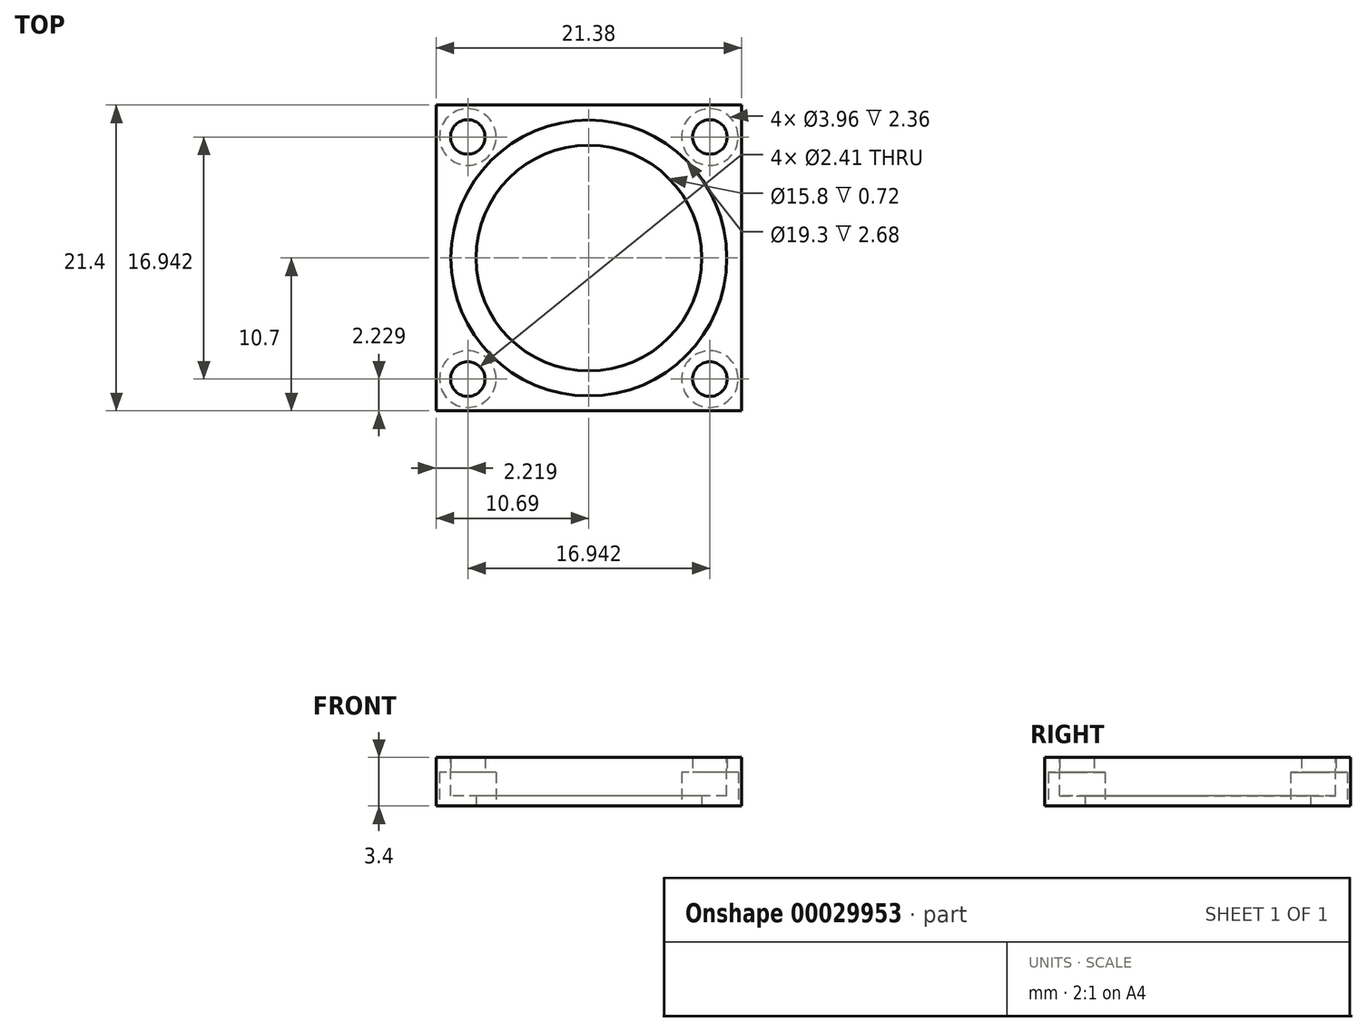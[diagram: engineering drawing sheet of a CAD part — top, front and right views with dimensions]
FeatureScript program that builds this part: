
annotation { "Feature Type Name" : "Feature", "Feature Type Description" : "" }
export const myFeature = defineFeature(function(context is Context, id is Id, definition is map)
    precondition{}
    {
        {
            var Q0;
            Q0=qCreatedBy(makeId("Top.planeOp"),FACE);
            var sketch = newSketch(context, id + "F0", { "sketchPlane" : qUnion([Q0])});
            skCircle(sketch, "E0", {"center": v(-8.47, 8.47) * mm, "radius": 1.2 * mm});
            skLineSegment(sketch, "E1.rect.bottom", {"start": v(-10.69, 10.7) * mm, "end": v(10.7, 10.7) * mm});
            skLineSegment(sketch, "E1.rect.top", {"start": v(-10.7, -10.7) * mm, "end": v(10.7, -10.7) * mm});
            skLineSegment(sketch, "E1.rect.left", {"start": v(-10.69, 10.7) * mm, "end": v(-10.7, -10.7) * mm});
            skLineSegment(sketch, "E1.rect.right", {"start": v(10.7, 10.7) * mm, "end": v(10.7, -10.7) * mm});
            skPoint(sketch, "E1.rect.middle", {"position": v(0, 0) * mm});
            skCircle(sketch, "E2", {"center": v(-8.47, 8.47) * mm, "radius": 1.98 * mm});
            skLineSegment(sketch, "E3.rect.bottom", {"start": v(-8.47, 8.47) * mm, "end": v(8.47, 8.47) * mm, "construction": true});
            skLineSegment(sketch, "E3.rect.top", {"start": v(-8.47, -8.47) * mm, "end": v(8.47, -8.47) * mm, "construction": true});
            skLineSegment(sketch, "E3.rect.left", {"start": v(-8.47, 8.47) * mm, "end": v(-8.47, -8.47) * mm, "construction": true});
            skLineSegment(sketch, "E3.rect.right", {"start": v(8.47, 8.47) * mm, "end": v(8.47, -8.47) * mm, "construction": true});
            skCircle(sketch, "E4.0.1.0", {"center": v(-8.47, -8.47) * mm, "radius": 1.2 * mm});
            skCircle(sketch, "E4.0.1.1", {"center": v(-8.47, -8.47) * mm, "radius": 1.98 * mm});
            skCircle(sketch, "E4.1.0.0", {"center": v(8.47, 8.47) * mm, "radius": 1.2 * mm});
            skCircle(sketch, "E4.1.0.1", {"center": v(8.47, 8.47) * mm, "radius": 1.98 * mm});
            skCircle(sketch, "E4.1.1.0", {"center": v(8.47, -8.47) * mm, "radius": 1.2 * mm});
            skCircle(sketch, "E4.1.1.1", {"center": v(8.47, -8.47) * mm, "radius": 1.98 * mm});
            skCircle(sketch, "E5", {"center": v(0, 0) * mm, "radius": 7.9 * mm});
            skSolve(sketch);
        }
        {
            var Q0;
            Q0=makeQuery(id+"F0.imprint","IMPRINT",FACE,{"disambiguationData":[TD([[makeQuery(id+"F0.imprint","IMPRINT",EDGE,{"derivedFrom":sQuery(id+"F0.wireOp",EDGE,"E1.rect.bottom")}),-1.0]])]});
            var Q1;
            Q1=makeQuery(id+"F0.imprint","IMPRINT",FACE,{"disambiguationData":[TD([[makeQuery(id+"F0.imprint","IMPRINT",EDGE,{"derivedFrom":sQuery(id+"F0.wireOp",EDGE,"E4.0.1.0")}),-1.0]])]});
            var Q2;
            Q2=makeQuery(id+"F0.imprint","IMPRINT",FACE,{"disambiguationData":[TD([[makeQuery(id+"F0.imprint","IMPRINT",EDGE,{"derivedFrom":sQuery(id+"F0.wireOp",EDGE,"E4.0.1.0")}),1.0]])]});
            var Q3;
            Q3=makeQuery(id+"F0.imprint","IMPRINT",FACE,{"disambiguationData":[TD([[makeQuery(id+"F0.imprint","IMPRINT",EDGE,{"derivedFrom":sQuery(id+"F0.wireOp",EDGE,"E4.1.1.0")}),1.0]])]});
            var Q4;
            Q4=makeQuery(id+"F0.imprint","IMPRINT",FACE,{"disambiguationData":[TD([[makeQuery(id+"F0.imprint","IMPRINT",EDGE,{"derivedFrom":sQuery(id+"F0.wireOp",EDGE,"E4.1.1.0")}),-1.0]])]});
            var Q5;
            Q5=makeQuery(id+"F0.imprint","IMPRINT",FACE,{"disambiguationData":[TD([[makeQuery(id+"F0.imprint","IMPRINT",EDGE,{"derivedFrom":sQuery(id+"F0.wireOp",EDGE,"E4.1.0.0")}),-1.0]])]});
            var Q6;
            Q6=makeQuery(id+"F0.imprint","IMPRINT",FACE,{"disambiguationData":[TD([[makeQuery(id+"F0.imprint","IMPRINT",EDGE,{"derivedFrom":sQuery(id+"F0.wireOp",EDGE,"E4.1.0.0")}),1.0]])]});
            var Q7;
            Q7=makeQuery(id+"F0.imprint","IMPRINT",FACE,{"disambiguationData":[TD([[makeQuery(id+"F0.imprint","IMPRINT",EDGE,{"derivedFrom":sQuery(id+"F0.wireOp",EDGE,"E0")}),1.0]])]});
            var Q8;
            Q8=makeQuery(id+"F0.imprint","IMPRINT",FACE,{"disambiguationData":[TD([[makeQuery(id+"F0.imprint","IMPRINT",EDGE,{"derivedFrom":sQuery(id+"F0.wireOp",EDGE,"E0")}),-1.0]])]});
            extrude(context, id + "F1", {"entities" : qUnion([Q0, Q1, Q2, Q3, Q4, Q5, Q6, Q7, Q8]), "depth" : 3.4 * mm});
        }
        {
            var Q0;
            Q0=makeQuery(id+"F0.imprint","IMPRINT",FACE,{"disambiguationData":[TD([[makeQuery(id+"F0.imprint","IMPRINT",EDGE,{"derivedFrom":sQuery(id+"F0.wireOp",EDGE,"E4.0.1.0")}),-1.0]])]});
            var Q1;
            Q1=makeQuery(id+"F0.imprint","IMPRINT",FACE,{"disambiguationData":[TD([[makeQuery(id+"F0.imprint","IMPRINT",EDGE,{"derivedFrom":sQuery(id+"F0.wireOp",EDGE,"E0")}),-1.0]])]});
            var Q2;
            Q2=makeQuery(id+"F0.imprint","IMPRINT",FACE,{"disambiguationData":[TD([[makeQuery(id+"F0.imprint","IMPRINT",EDGE,{"derivedFrom":sQuery(id+"F0.wireOp",EDGE,"E4.1.1.0")}),-1.0]])]});
            var Q3;
            Q3=makeQuery(id+"F0.imprint","IMPRINT",FACE,{"disambiguationData":[TD([[makeQuery(id+"F0.imprint","IMPRINT",EDGE,{"derivedFrom":sQuery(id+"F0.wireOp",EDGE,"E4.1.0.0")}),-1.0]])]});
            var Q4;
            Q4=makeQuery(id+"F0.imprint","IMPRINT",FACE,{"disambiguationData":[TD([[makeQuery(id+"F0.imprint","IMPRINT",EDGE,{"derivedFrom":sQuery(id+"F0.wireOp",EDGE,"E4.0.1.0")}),1.0]])]});
            var Q5;
            Q5=makeQuery(id+"F0.imprint","IMPRINT",FACE,{"disambiguationData":[TD([[makeQuery(id+"F0.imprint","IMPRINT",EDGE,{"derivedFrom":sQuery(id+"F0.wireOp",EDGE,"E4.1.1.0")}),1.0]])]});
            var Q6;
            Q6=makeQuery(id+"F0.imprint","IMPRINT",FACE,{"disambiguationData":[TD([[makeQuery(id+"F0.imprint","IMPRINT",EDGE,{"derivedFrom":sQuery(id+"F0.wireOp",EDGE,"E0")}),1.0]])]});
            var Q7;
            Q7=makeQuery(id+"F0.imprint","IMPRINT",FACE,{"disambiguationData":[TD([[makeQuery(id+"F0.imprint","IMPRINT",EDGE,{"derivedFrom":sQuery(id+"F0.wireOp",EDGE,"E4.1.0.0")}),1.0]])]});
            extrude(context, id + "F2", {"entities" : qUnion([Q0, Q1, Q2, Q3, Q4, Q5, Q6, Q7]), "operationType" : NewBodyOperationType.REMOVE, "depth" : 2.36 * mm});
        }
        {
            var Q0;
            Q0=makeQuery(id+"F0.imprint","IMPRINT",FACE,{"disambiguationData":[TD([[makeQuery(id+"F0.imprint","IMPRINT",EDGE,{"derivedFrom":sQuery(id+"F0.wireOp",EDGE,"E4.0.1.0")}),1.0]])]});
            var Q1;
            Q1=makeQuery(id+"F0.imprint","IMPRINT",FACE,{"disambiguationData":[TD([[makeQuery(id+"F0.imprint","IMPRINT",EDGE,{"derivedFrom":sQuery(id+"F0.wireOp",EDGE,"E4.1.1.0")}),1.0]])]});
            var Q2;
            Q2=makeQuery(id+"F0.imprint","IMPRINT",FACE,{"disambiguationData":[TD([[makeQuery(id+"F0.imprint","IMPRINT",EDGE,{"derivedFrom":sQuery(id+"F0.wireOp",EDGE,"E4.1.0.0")}),1.0]])]});
            var Q3;
            Q3=makeQuery(id+"F0.imprint","IMPRINT",FACE,{"disambiguationData":[TD([[makeQuery(id+"F0.imprint","IMPRINT",EDGE,{"derivedFrom":sQuery(id+"F0.wireOp",EDGE,"E0")}),1.0]])]});
            extrude(context, id + "F3", {"entities" : qUnion([Q0, Q1, Q2, Q3]), "operationType" : NewBodyOperationType.REMOVE, "endBound" : BoundingType.THROUGH_ALL, "depth" : 25 * mm});
        }
        {
            var Q0;
            Q0=makeQuery(id+"F1.opExtrude","CAP_FACE",FACE,{"disambiguationData":[OSD([sQuery(id+"F0.wireOp",EDGE,"E1.rect.bottom"),sQuery(id+"F0.wireOp",EDGE,"E1.rect.top"),sQuery(id+"F0.wireOp",EDGE,"E1.rect.left"),sQuery(id+"F0.wireOp",EDGE,"E1.rect.right"),sQuery(id+"F0.wireOp",EDGE,"E5")])],"isStart":false});
            var sketch = newSketch(context, id + "F4", { "sketchPlane" : qUnion([Q0])});
            skCircle(sketch, "E6", {"center": v(0, 0) * mm, "radius": 9.65 * mm});
            skSolve(sketch);
        }
        {
            var Q0;
            Q0=makeQuery(id+"F4.imprint","IMPRINT",FACE,{"disambiguationData":[TD([[makeQuery(id+"F4.imprint","IMPRINT",EDGE,{"derivedFrom":sQuery(id+"F4.wireOp",EDGE,"E6")}),1.0]])]});
            extrude(context, id + "F5", {"entities" : qUnion([Q0]), "operationType" : NewBodyOperationType.REMOVE, "oppositeDirection" : true, "depth" : 2.68 * mm});
        }
    });
